FCSTD DOCUMENT  (FreeCAD 0.21R30454 (Git))
Label: WingTest
License: All rights reserved
LicenseURL: http://en.wikipedia.org/wiki/All_rights_reserved
objects: Spreadsheet::Sheet×2, Sketcher::SketchObject×1
note: 1 computed .brp shape members not serialized (recipe doc carries the construction recipe); baked Part::Feature solids carry a one-line shape summary decoded from their .brp

FEATURE [Spreadsheet::Sheet] Spreadsheet
  cells = A2=crank_r; B2(crank_r)=5; A3=crank_edge_off_pcb; B3(crank_edge_off_pcb)=4; A4=motor_h; B4(motor_h)==crank_r + crank_edge_off_pcb; A5=hinge_dist_from_motor; B5(hinge_dist_from_motor)=20; A6=conn_rod_l; B6(conn_rod_l)=25; A7=pivot_d; B7(pivot_d)=9; B8==pivot_d
FEATURE [Spreadsheet::Sheet] Spreadsheet001
FEATURE [Sketcher::SketchObject] Sketch
  FullyConstrained = false
  expr: Constraints[10] = Spreadsheet.conn_rod_l
  expr: Constraints[3] = Spreadsheet.pivot_d
  expr: Constraints[4] = Spreadsheet.hinge_dist_from_motor
  expr: Constraints[5] = Spreadsheet.crank_r
  expr: Constraints[6] = Spreadsheet.motor_h
  sketch-geometry (5):
    g0: Circle CenterX=0 CenterY=9 CenterZ=0 NormalX=0 NormalY=0 NormalZ=1 AngleXU=0 Radius=5
    g1: LineSegment StartX=20 StartY=0 StartZ=0 EndX=115.166 EndY=115.946 EndZ=0
    g2: GeomPoint X=25.71 Y=6.95674 Z=0
    g3: GeomPoint X=1.64285 Y=13.7224 Z=0
    g4: LineSegment StartX=1.64285 StartY=13.7224 StartZ=0 EndX=25.71 EndY=6.95674 EndZ=0
  constraints (12):
    c: PointOnObject(g0,g-2)
    c: PointOnObject(g1,g-1)
    c: PointOnObject(g2,g1)
    c: Distance(g1,g2) = 9
    c: DistanceX(g-1,g1) = 20
    c: Radius(g0) = 5
    c: DistanceY(g-1,g0) = 9
    c: Distance(g1) = 150
    c: Coincident(g4,g3)
    c: Coincident(g4,g2)
    c: Distance(g4) = 25
    c: PointOnObject(g4,g0)
